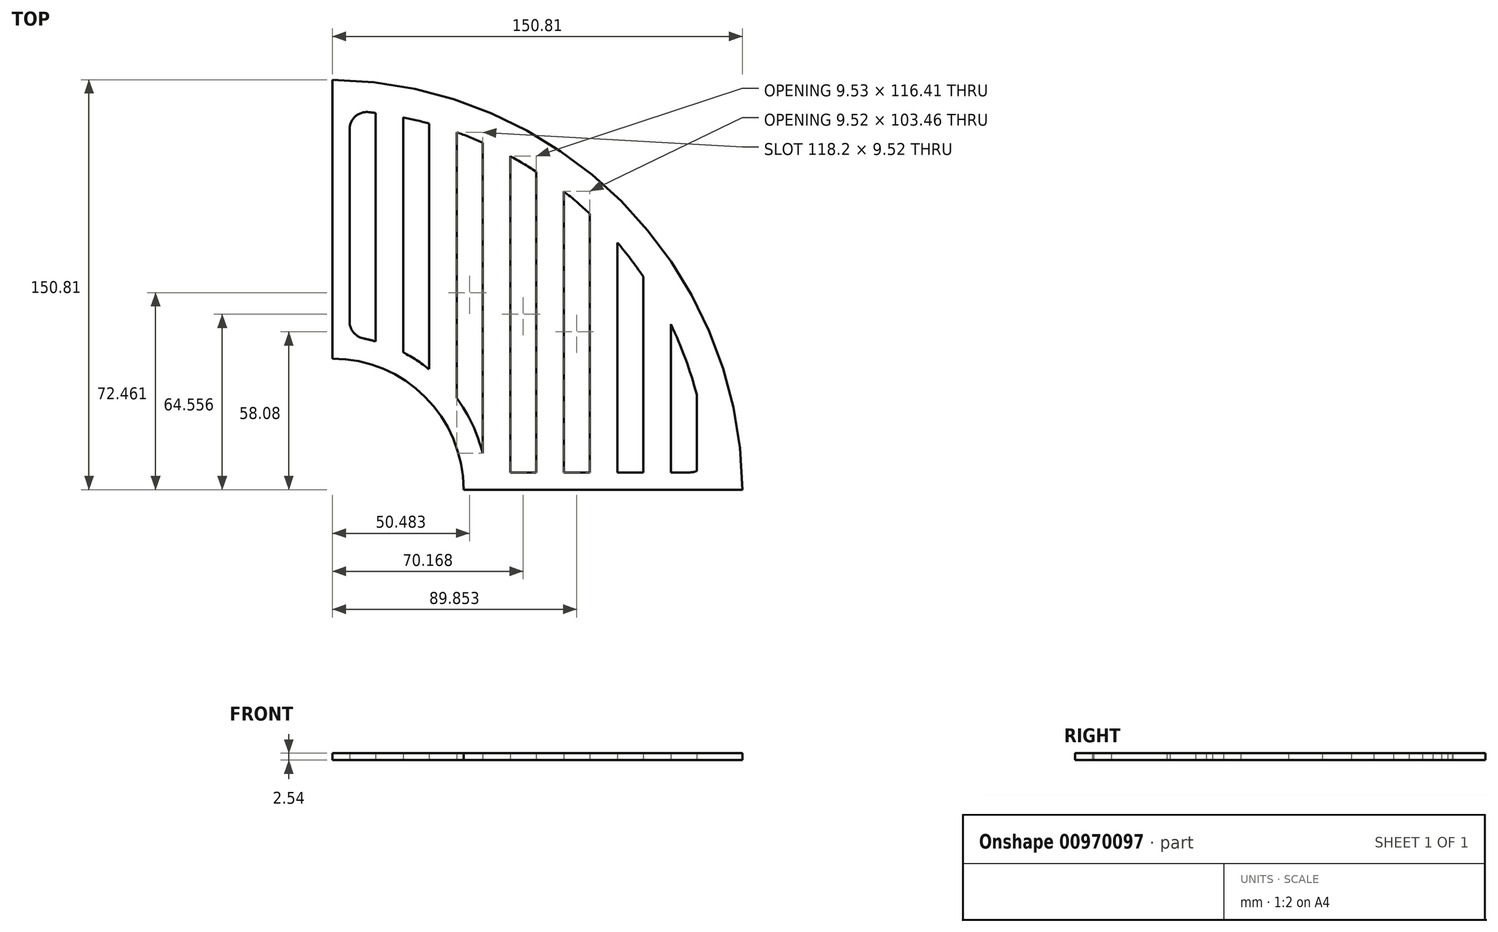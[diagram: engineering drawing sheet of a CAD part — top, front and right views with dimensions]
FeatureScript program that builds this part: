
annotation { "Feature Type Name" : "Feature", "Feature Type Description" : "" }
export const myFeature = defineFeature(function(context is Context, id is Id, definition is map)
    precondition{}
    {
        {
            var Q0;
            Q0=qCreatedBy(makeId("Top.planeOp"),FACE);
            var sketch = newSketch(context, id + "F0", { "sketchPlane" : qUnion([Q0])});
            skLineSegment(sketch, "E0", {"start": v(6.35, 61.9) * mm, "end": v(6.35, 132.62) * mm});
            skLineSegment(sketch, "E1", {"start": v(65.4, 6.35) * mm, "end": v(74.93, 6.35) * mm});
            skArc(sketch, "E2", {"start": v(55.25, 13.36) * mm, "mid": v(51.5, 24.04) * mm, "end": v(45.72, 33.77) * mm});
            skArc(sketch, "E3", {"start": v(133.99, 34.96) * mm, "mid": v(129.87, 48.16) * mm, "end": v(124.46, 60.9) * mm});
            skPoint(sketch, "E4.visualSharp", {"position": v(6.35, 139.5) * mm});
            skArc(sketch, "E4.filletArc", {"start": v(13.37, 138.93) * mm, "mid": v(8.45, 137.34) * mm, "end": v(6.35, 132.62) * mm});
            skPoint(sketch, "E5.visualSharp", {"position": v(138.29, 6.35) * mm});
            skArc(sketch, "E5.filletArc", {"start": v(131.47, 6.35) * mm, "mid": v(132.76, 6.48) * mm, "end": v(133.99, 6.87) * mm});
            skPoint(sketch, "E6.visualSharp", {"position": v(56.48, 6.35) * mm});
            skPoint(sketch, "E7.visualSharp", {"position": v(6.35, 56.48) * mm});
            skArc(sketch, "E7.filletArc", {"start": v(6.35, 61.9) * mm, "mid": v(7.78, 57.89) * mm, "end": v(11.42, 55.68) * mm});
            skPoint(sketch, "E8", {"position": v(6.35, 61.9) * mm});
            skLineSegment(sketch, "E9", {"start": v(0, 0) * mm, "end": v(150.81, 0) * mm});
            skLineSegment(sketch, "E10", {"start": v(0, 0) * mm, "end": v(0, 150.81) * mm});
            skArc(sketch, "E11", {"start": v(150.81, 0) * mm, "mid": v(106.18, 106.18) * mm, "end": v(0, 150.81) * mm});
            skLineSegment(sketch, "E12", {"start": v(0, 150.81) * mm, "end": v(0, 150.81) * mm});
            skLineSegment(sketch, "E13", {"start": v(150.81, 0) * mm, "end": v(150.81, 0) * mm});
            skArc(sketch, "E14", {"start": v(0, 48.26) * mm, "mid": v(34.12, 34.12) * mm, "end": v(48.26, 0) * mm});
            skLineSegment(sketch, "E15.trimOffspring", {"start": v(26.04, 50.52) * mm, "end": v(26.03, 137) * mm});
            skLineSegment(sketch, "E16.trimOffspring", {"start": v(15.87, 54.58) * mm, "end": v(15.87, 138.64) * mm});
            skArc(sketch, "E17.trimOffspring", {"start": v(15.87, 54.58) * mm, "mid": v(13.66, 55.17) * mm, "end": v(11.42, 55.68) * mm});
            skArc(sketch, "E18.trimOffspring", {"start": v(15.87, 138.64) * mm, "mid": v(14.62, 138.8) * mm, "end": v(13.37, 138.93) * mm});
            skPoint(sketch, "E19.oppositeSnap0", {"position": v(45.72, 33.77) * mm});
            skLineSegment(sketch, "E19.right", {"start": v(45.72, 131.56) * mm, "end": v(45.72, 33.77) * mm});
            skArc(sketch, "E20.trimOffspring", {"start": v(35.56, 134.76) * mm, "mid": v(30.82, 135.97) * mm, "end": v(26.04, 137) * mm});
            skLineSegment(sketch, "E21.trimOffspring", {"start": v(35.56, 134.76) * mm, "end": v(35.56, 44.34) * mm});
            skPoint(sketch, "E22.orphan", {"position": v(45.72, 20.4) * mm});
            skArc(sketch, "E23.trimOffspring", {"start": v(35.56, 44.34) * mm, "mid": v(30.95, 47.67) * mm, "end": v(26.03, 50.52) * mm});
            skLineSegment(sketch, "E24.trimOffspring", {"start": v(65.4, 122.76) * mm, "end": v(65.4, 6.35) * mm});
            skLineSegment(sketch, "E25.trimOffspring", {"start": v(55.24, 127.76) * mm, "end": v(55.25, 13.36) * mm});
            skArc(sketch, "E26.trimOffspring", {"start": v(55.24, 127.76) * mm, "mid": v(50.52, 129.75) * mm, "end": v(45.72, 131.56) * mm});
            skLineSegment(sketch, "E27.trimOffspring", {"start": v(85.1, 6.35) * mm, "end": v(94.62, 6.35) * mm});
            skLineSegment(sketch, "E28.trimOffspring", {"start": v(85.09, 109.8) * mm, "end": v(85.1, 6.35) * mm});
            skLineSegment(sketch, "E29.trimOffspring", {"start": v(74.93, 117.09) * mm, "end": v(74.93, 6.35) * mm});
            skArc(sketch, "E30.trimOffspring", {"start": v(74.93, 117.09) * mm, "mid": v(70.22, 120.02) * mm, "end": v(65.4, 122.76) * mm});
            skLineSegment(sketch, "E31.left", {"start": v(94.62, 101.6) * mm, "end": v(94.62, 6.35) * mm});
            skLineSegment(sketch, "E31.right", {"start": v(104.78, 90.94) * mm, "end": v(104.78, 6.35) * mm});
            skArc(sketch, "E32.trimOffspring", {"start": v(94.61, 101.6) * mm, "mid": v(89.94, 105.81) * mm, "end": v(85.09, 109.8) * mm});
            skLineSegment(sketch, "E33.trimOffspring", {"start": v(104.78, 6.35) * mm, "end": v(114.3, 6.35) * mm});
            skLineSegment(sketch, "E34.left", {"start": v(114.3, 78.48) * mm, "end": v(114.3, 6.35) * mm});
            skLineSegment(sketch, "E34.right", {"start": v(124.46, 60.9) * mm, "end": v(124.46, 6.35) * mm});
            skArc(sketch, "E35.trimOffspring", {"start": v(114.3, 78.48) * mm, "mid": v(109.71, 84.85) * mm, "end": v(104.78, 90.94) * mm});
            skLineSegment(sketch, "E36.trimOffspring", {"start": v(124.46, 6.35) * mm, "end": v(131.47, 6.35) * mm});
            skLineSegment(sketch, "E37.left", {"start": v(133.99, 34.96) * mm, "end": v(133.99, 6.87) * mm});
            skSolve(sketch);
        }
        {
            var Q0;
            Q0=makeQuery(id+"F0.imprint","IMPRINT",FACE,{"disambiguationData":[TD([[makeQuery(id+"F0.imprint","IMPRINT",EDGE,{"derivedFrom":sQuery(id+"F0.wireOp",EDGE,"E0")}),1.0]])]});
            extrude(context, id + "F1", {"entities" : qUnion([Q0]), "depth" : 2.54 * mm, "offsetDistance" : 25.4 * mm});
        }
    });
